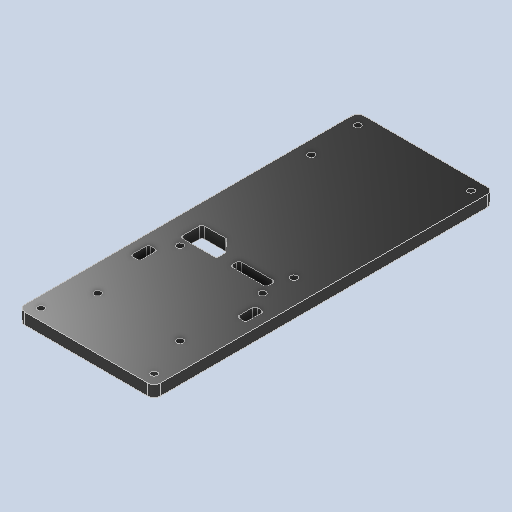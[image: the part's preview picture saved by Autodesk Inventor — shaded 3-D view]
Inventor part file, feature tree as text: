
AUTODESK INVENTOR PART (.ipt)
format: ipt  version: 2023 (Build 270158000, 158)  size: 180,736 bytes
history: native  units: in
note: dims shown in document units (in); Inventor stores cm internally (conversion verified against a paired STEP export)
features: other x3, sketch x1
ambient origin geometry x8: Origin, YZ Plane, XZ Plane, XY Plane, X Axis, Y Axis, Z Axis, Center Point
bodies: Solid1 (feature_tree)
feature tree (4):
  other  "DeGiua.ipt"
  other  "Solid1::DeGiua.ipt"
  other  "TaggingFeature1"
  sketch  "Sketch1"  dims[d0=0.3937in]
